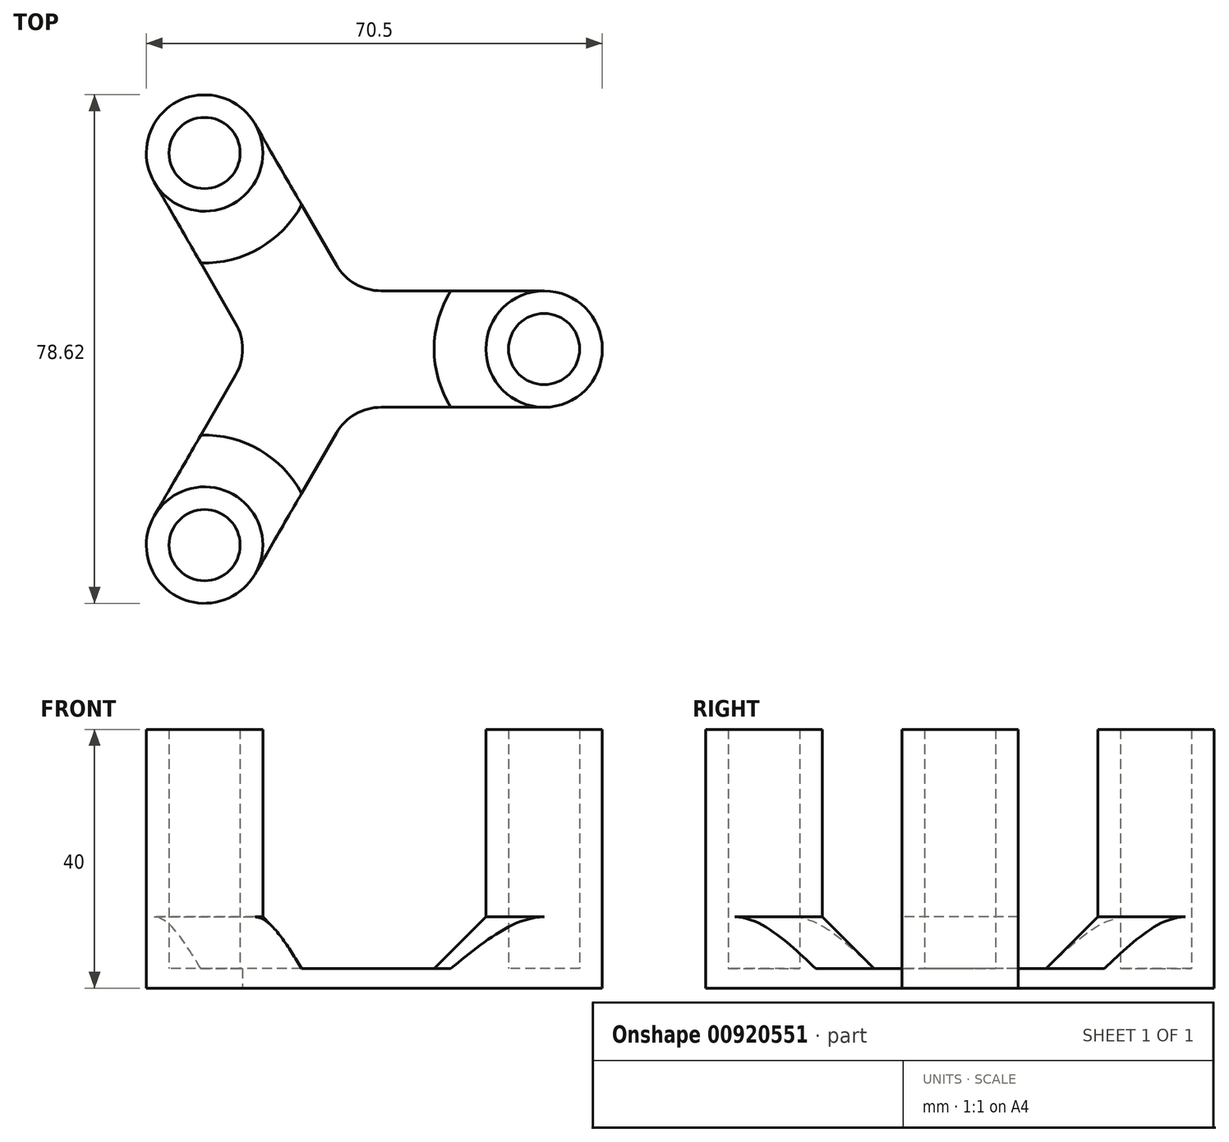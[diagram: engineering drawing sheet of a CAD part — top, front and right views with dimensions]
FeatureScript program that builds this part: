
annotation { "Feature Type Name" : "Feature", "Feature Type Description" : "" }
export const myFeature = defineFeature(function(context is Context, id is Id, definition is map)
    precondition{}
    {
        {
            var Q0;
            Q0=qCreatedBy(makeId("Top.planeOp"),FACE);
            var sketch = newSketch(context, id + "F0", { "sketchPlane" : qUnion([Q0])});
            skLineSegment(sketch, "E0", {"start": v(0, 0) * mm, "end": v(70, 0) * mm, "construction": true});
            skPoint(sketch, "E1.center", {"position": v(0, 0) * mm});
            skPoint(sketch, "E2", {"position": v(35, 0) * mm});
            skCircle(sketch, "E3", {"center": v(35, 0) * mm, "radius": 5.5 * mm});
            skCircle(sketch, "E4", {"center": v(35, 0) * mm, "radius": 9 * mm});
            skLineSegment(sketch, "E5", {"start": v(35, 9) * mm, "end": v(5.2, 9) * mm});
            skLineSegment(sketch, "E6", {"start": v(35, -9) * mm, "end": v(5.2, -9) * mm});
            skCircle(sketch, "E7.1.0", {"center": v(-17.5, 30.31) * mm, "radius": 5.5 * mm});
            skCircle(sketch, "E7.1.1", {"center": v(-17.5, 30.31) * mm, "radius": 9 * mm});
            skLineSegment(sketch, "E7.1.2", {"start": v(-25.3, 25.81) * mm, "end": v(-10.4, 0) * mm});
            skLineSegment(sketch, "E7.1.3", {"start": v(-9.7, 34.81) * mm, "end": v(5.2, 9) * mm});
            skCircle(sketch, "E7.2.0", {"center": v(-17.5, -30.31) * mm, "radius": 5.5 * mm});
            skCircle(sketch, "E7.2.1", {"center": v(-17.5, -30.31) * mm, "radius": 9 * mm});
            skLineSegment(sketch, "E7.2.2", {"start": v(-9.7, -34.81) * mm, "end": v(5.2, -9) * mm});
            skLineSegment(sketch, "E7.2.3", {"start": v(-25.3, -25.81) * mm, "end": v(-10.4, 0) * mm});
            skPoint(sketch, "E8.orphan", {"position": v(7.8, 4.5) * mm});
            skPoint(sketch, "E9.orphan", {"position": v(0, 9) * mm});
            skPoint(sketch, "E10.orphan", {"position": v(-7.8, 4.5) * mm});
            skPoint(sketch, "E11.orphan", {"position": v(-7.8, -4.5) * mm});
            skPoint(sketch, "E12.orphan", {"position": v(7.8, -4.5) * mm});
            skPoint(sketch, "E13.orphan", {"position": v(0, -9) * mm});
            skCircle(sketch, "E14", {"center": v(0, 0) * mm, "radius": 9 * mm});
            skSolve(sketch);
        }
        {
            var Q0;
            Q0=makeQuery(id+"F0.imprint","IMPRINT",FACE,{"disambiguationData":[TD([[makeQuery(id+"F0.imprint","IMPRINT",EDGE,{"derivedFrom":sQuery(id+"F0.wireOp",EDGE,"E7.1.0")}),-1.0]])]});
            var Q1;
            {var subQ1=sQuery(id+"F0.wireOp",EDGE,"E5");Q1=makeQuery(id+"F0.imprint","IMPRINT",FACE,{"disambiguationData":[TD([[makeQuery(id+"F0.imprint","IMPRINT",EDGE,{"derivedFrom":subQ1}),1.0]])]});}
            var Q2;
            Q2=makeQuery(id+"F0.imprint","IMPRINT",FACE,{"disambiguationData":[TD([[makeQuery(id+"F0.imprint","IMPRINT",EDGE,{"derivedFrom":sQuery(id+"F0.wireOp",EDGE,"E14")}),1.0]])]});
            var Q3;
            Q3=makeQuery(id+"F0.imprint","IMPRINT",FACE,{"disambiguationData":[TD([[makeQuery(id+"F0.imprint","IMPRINT",EDGE,{"derivedFrom":sQuery(id+"F0.wireOp",EDGE,"E7.1.0")}),1.0]])]});
            var Q4;
            Q4=makeQuery(id+"F0.imprint","IMPRINT",FACE,{"disambiguationData":[TD([[makeQuery(id+"F0.imprint","IMPRINT",EDGE,{"derivedFrom":sQuery(id+"F0.wireOp",EDGE,"E7.2.0")}),1.0]])]});
            var Q5;
            Q5=makeQuery(id+"F0.imprint","IMPRINT",FACE,{"disambiguationData":[TD([[makeQuery(id+"F0.imprint","IMPRINT",EDGE,{"derivedFrom":sQuery(id+"F0.wireOp",EDGE,"E7.2.0")}),-1.0]])]});
            var Q6;
            Q6=makeQuery(id+"F0.imprint","IMPRINT",FACE,{"disambiguationData":[TD([[makeQuery(id+"F0.imprint","IMPRINT",EDGE,{"derivedFrom":sQuery(id+"F0.wireOp",EDGE,"E3")}),-1.0]])]});
            var Q7;
            Q7=makeQuery(id+"F0.imprint","IMPRINT",FACE,{"disambiguationData":[TD([[makeQuery(id+"F0.imprint","IMPRINT",EDGE,{"derivedFrom":sQuery(id+"F0.wireOp",EDGE,"E3")}),1.0]])]});
            extrude(context, id + "F1", {"entities" : qUnion([Q0, Q1, Q2, Q3, Q4, Q5, Q6, Q7]), "depth" : 3 * mm, "offsetDistance" : 25 * mm});
        }
        {
            var Q0;
            Q0=makeQuery(id+"F0.imprint","IMPRINT",FACE,{"disambiguationData":[TD([[makeQuery(id+"F0.imprint","IMPRINT",EDGE,{"derivedFrom":sQuery(id+"F0.wireOp",EDGE,"E7.1.0")}),-1.0]])]});
            var Q1;
            Q1=makeQuery(id+"F0.imprint","IMPRINT",FACE,{"disambiguationData":[TD([[makeQuery(id+"F0.imprint","IMPRINT",EDGE,{"derivedFrom":sQuery(id+"F0.wireOp",EDGE,"E3")}),-1.0]])]});
            var Q2;
            Q2=makeQuery(id+"F0.imprint","IMPRINT",FACE,{"disambiguationData":[TD([[makeQuery(id+"F0.imprint","IMPRINT",EDGE,{"derivedFrom":sQuery(id+"F0.wireOp",EDGE,"E7.2.0")}),-1.0]])]});
            extrude(context, id + "F2", {"entities" : qUnion([Q0, Q1, Q2]), "operationType" : NewBodyOperationType.ADD, "depth" : 40 * mm, "offsetDistance" : 25 * mm});
        }
        {
            var Q0;
            {var subQ0=sQuery(id+"F0.wireOp",EDGE,"E4");Q0=makeQuery(id+"F2.boolean.opBoolean","INTERSECT",EDGE,{"derivedFrom":[makeQuery(id+"F1.opExtrude","CAP_FACE",FACE,{"disambiguationData":[OSD([subQ0,sQuery(id+"F0.wireOp",EDGE,"E5"),sQuery(id+"F0.wireOp",EDGE,"E6"),sQuery(id+"F0.wireOp",EDGE,"E7.1.1"),sQuery(id+"F0.wireOp",EDGE,"E7.1.2"),sQuery(id+"F0.wireOp",EDGE,"E7.1.3"),sQuery(id+"F0.wireOp",EDGE,"E7.2.1"),sQuery(id+"F0.wireOp",EDGE,"E7.2.2"),sQuery(id+"F0.wireOp",EDGE,"E7.2.3")])],"isStart":false}),makeQuery(id+"F2.opExtrude","SWEPT_FACE",FACE,{"disambiguationData":[OSD([subQ0])]})]});}
            var Q1;
            {var subQ0=sQuery(id+"F0.wireOp",EDGE,"E7.2.1");Q1=makeQuery(id+"F2.boolean.opBoolean","INTERSECT",EDGE,{"derivedFrom":[makeQuery(id+"F1.opExtrude","CAP_FACE",FACE,{"disambiguationData":[OSD([sQuery(id+"F0.wireOp",EDGE,"E4"),sQuery(id+"F0.wireOp",EDGE,"E5"),sQuery(id+"F0.wireOp",EDGE,"E6"),sQuery(id+"F0.wireOp",EDGE,"E7.1.1"),sQuery(id+"F0.wireOp",EDGE,"E7.1.2"),sQuery(id+"F0.wireOp",EDGE,"E7.1.3"),subQ0,sQuery(id+"F0.wireOp",EDGE,"E7.2.2"),sQuery(id+"F0.wireOp",EDGE,"E7.2.3")])],"isStart":false}),makeQuery(id+"F2.opExtrude","SWEPT_FACE",FACE,{"disambiguationData":[OSD([subQ0])]})]});}
            var Q2;
            {var subQ0=sQuery(id+"F0.wireOp",EDGE,"E7.1.1");Q2=makeQuery(id+"F2.boolean.opBoolean","INTERSECT",EDGE,{"derivedFrom":[makeQuery(id+"F1.opExtrude","CAP_FACE",FACE,{"disambiguationData":[OSD([sQuery(id+"F0.wireOp",EDGE,"E4"),sQuery(id+"F0.wireOp",EDGE,"E5"),sQuery(id+"F0.wireOp",EDGE,"E6"),subQ0,sQuery(id+"F0.wireOp",EDGE,"E7.1.2"),sQuery(id+"F0.wireOp",EDGE,"E7.1.3"),sQuery(id+"F0.wireOp",EDGE,"E7.2.1"),sQuery(id+"F0.wireOp",EDGE,"E7.2.2"),sQuery(id+"F0.wireOp",EDGE,"E7.2.3")])],"isStart":false}),makeQuery(id+"F2.opExtrude","SWEPT_FACE",FACE,{"disambiguationData":[OSD([subQ0])]})]});}
            chamfer(context, id + "F3", {"entities" : qUnion([Q0, Q1, Q2]), "width" : 8 * mm, "tangentPropagation" : true});
        }
        {
            var Q0;
            Q0=makeQuery(id+"F1.opExtrude","SWEPT_EDGE",EDGE,{"disambiguationData":[OSD([sQuery(id+"F0.wireOp",EDGE,"E6"),sQuery(id+"F0.wireOp",EDGE,"E7.2.2")])]});
            var Q1;
            Q1=makeQuery(id+"F1.opExtrude","SWEPT_EDGE",EDGE,{"disambiguationData":[OSD([sQuery(id+"F0.wireOp",EDGE,"E5"),sQuery(id+"F0.wireOp",EDGE,"E7.1.3")])]});
            var Q2;
            Q2=makeQuery(id+"F1.opExtrude","SWEPT_EDGE",EDGE,{"disambiguationData":[OSD([sQuery(id+"F0.wireOp",EDGE,"E7.1.2"),sQuery(id+"F0.wireOp",EDGE,"E7.2.3")])]});
            fillet(context, id + "F4", {"entities" : qUnion([Q0, Q1, Q2]), "radius" : 8 * mm, "tangentPropagation" : true, "allowEdgeOverflow" : false});
        }
    });
